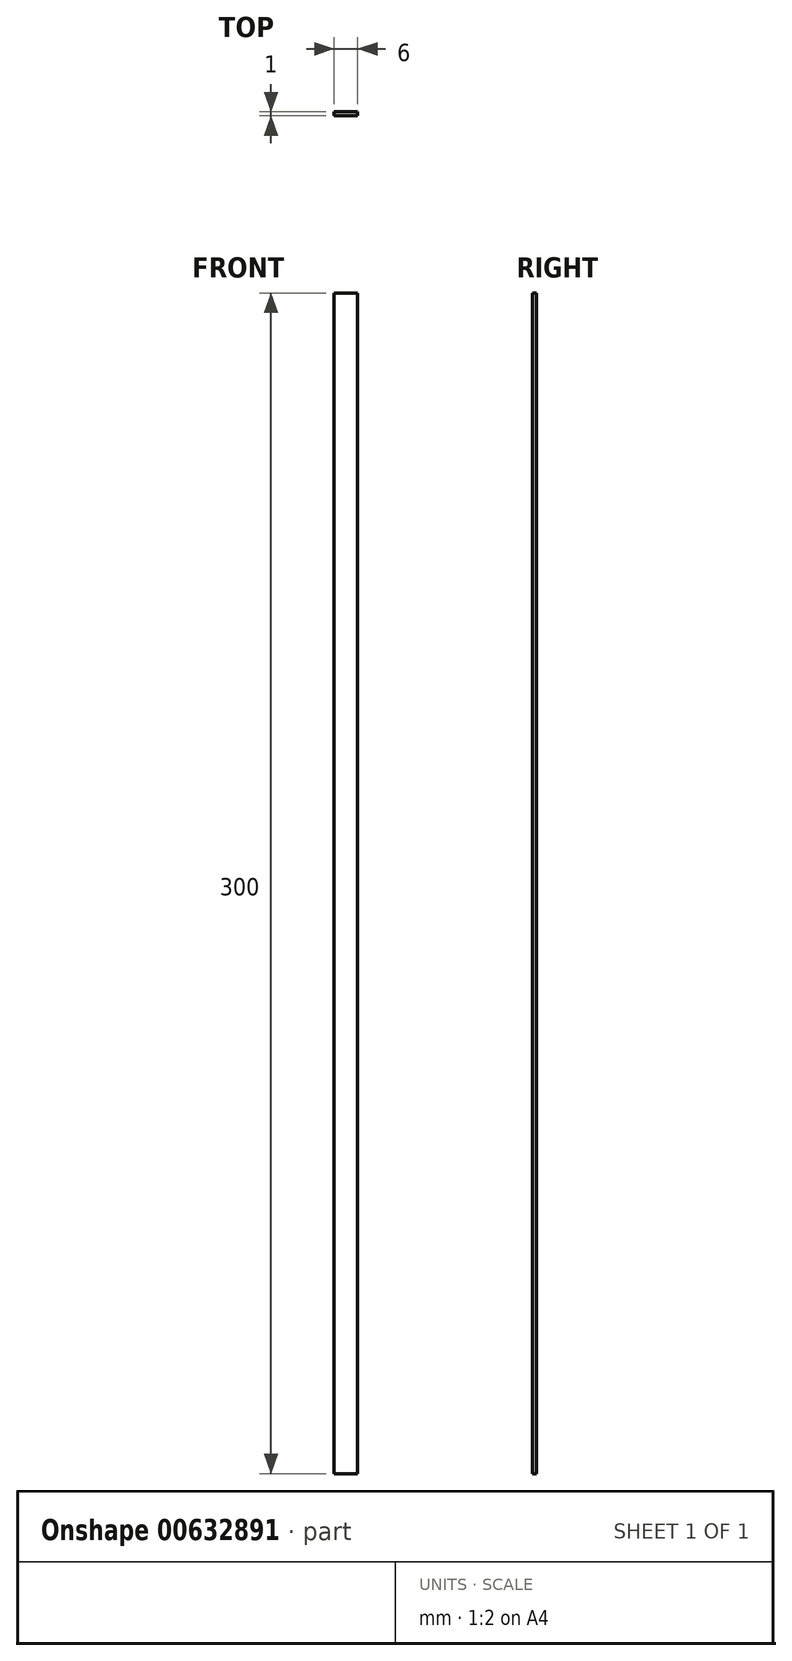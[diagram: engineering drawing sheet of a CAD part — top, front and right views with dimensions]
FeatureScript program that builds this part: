
annotation { "Feature Type Name" : "Feature", "Feature Type Description" : "" }
export const myFeature = defineFeature(function(context is Context, id is Id, definition is map)
    precondition{}
    {
        {
            var Q0;
            Q0=qCreatedBy(makeId("Top.planeOp"),FACE);
            var sketch = newSketch(context, id + "F0", { "sketchPlane" : qUnion([Q0])});
            skLineSegment(sketch, "E0.bottom", {"start": v(3, -0.5) * mm, "end": v(-3, -0.5) * mm});
            skLineSegment(sketch, "E0.top", {"start": v(3, 0.5) * mm, "end": v(-3, 0.5) * mm});
            skLineSegment(sketch, "E0.left", {"start": v(3, -0.5) * mm, "end": v(3, 0.5) * mm});
            skLineSegment(sketch, "E0.right", {"start": v(-3, -0.5) * mm, "end": v(-3, 0.5) * mm});
            skPoint(sketch, "E0.middle", {"position": v(0, 0) * mm});
            skSolve(sketch);
        }
        {
            var Q0;
            Q0=makeQuery(id+"F0.imprint","IMPRINT",FACE,{"disambiguationData":[TD([[makeQuery(id+"F0.imprint","IMPRINT",EDGE,{"derivedFrom":sQuery(id+"F0.wireOp",EDGE,"E0.bottom")}),-1.0]])]});
            extrude(context, id + "F1", {"entities" : qUnion([Q0]), "depth" : 300 * mm});
        }
    });
